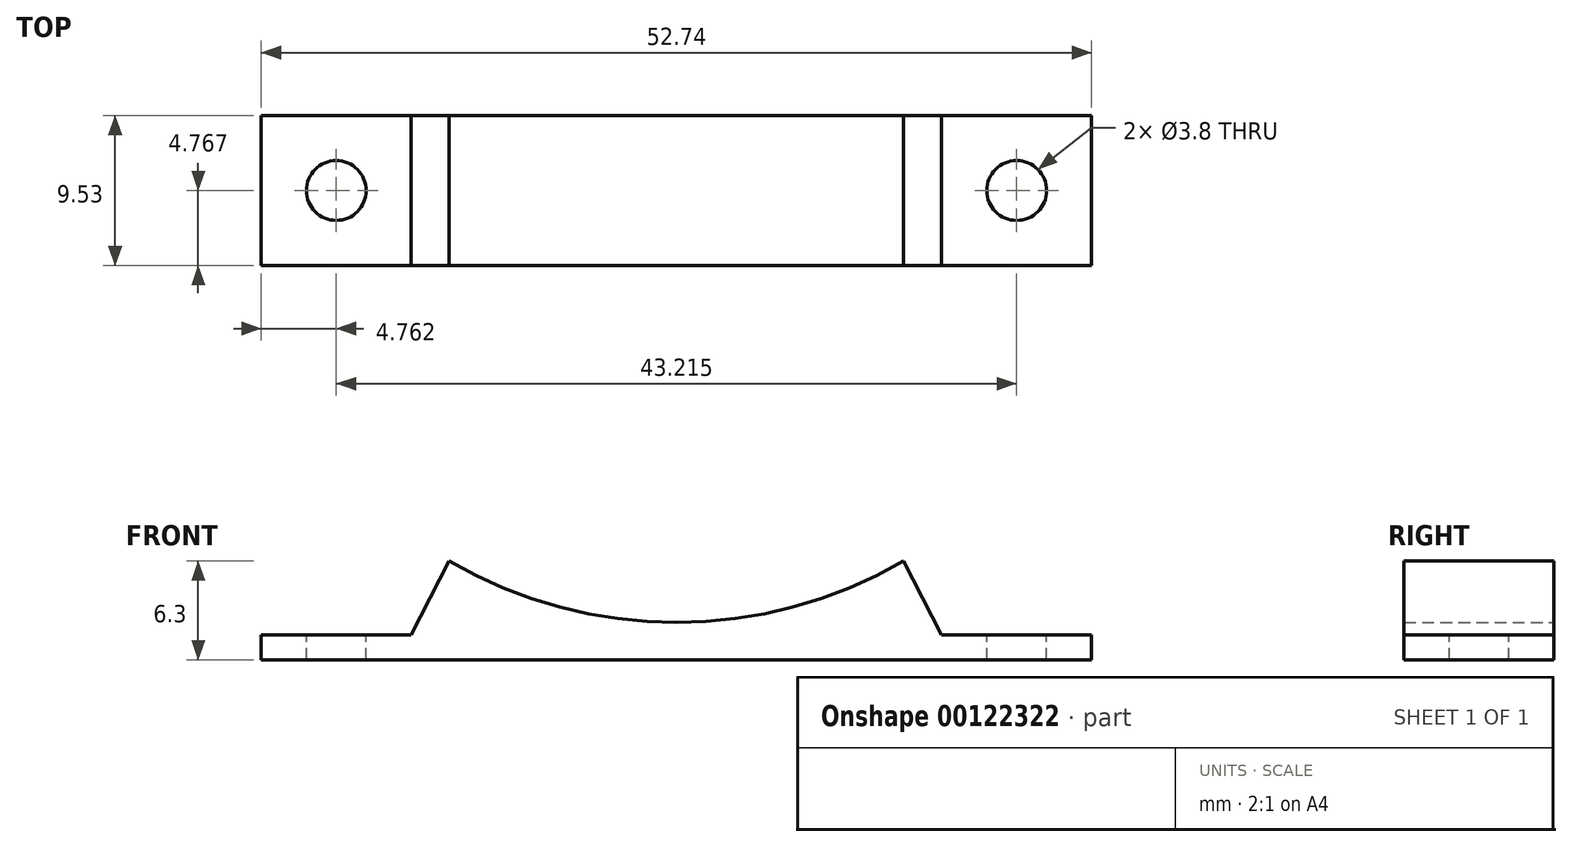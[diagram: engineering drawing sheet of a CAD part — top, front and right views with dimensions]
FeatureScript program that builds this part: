
annotation { "Feature Type Name" : "Feature", "Feature Type Description" : "" }
export const myFeature = defineFeature(function(context is Context, id is Id, definition is map)
    precondition{}
    {
        {
            var Q0;
            Q0=qCreatedBy(makeId("Front.planeOp"),FACE);
            var sketch = newSketch(context, id + "F0", { "sketchPlane" : qUnion([Q0])});
            skCircle(sketch, "E0", {"center": v(0, 0) * mm, "radius": 28.58 * mm});
            skLineSegment(sketch, "E1", {"start": v(0, -30.96) * mm, "end": v(-15.88, -30.96) * mm});
            skLineSegment(sketch, "E2", {"start": v(0, -30.96) * mm, "end": v(15.88, -30.96) * mm});
            skLineSegment(sketch, "E3", {"start": v(15.88, -30.96) * mm, "end": v(0, 0) * mm});
            skLineSegment(sketch, "E4", {"start": v(-15.88, -30.96) * mm, "end": v(0, 0) * mm});
            skLineSegment(sketch, "E5", {"start": v(-15.88, -30.96) * mm, "end": v(-26.37, -30.96) * mm});
            skLineSegment(sketch, "E6", {"start": v(-26.37, -30.96) * mm, "end": v(-26.37, -29.37) * mm});
            skLineSegment(sketch, "E7", {"start": v(-26.37, -29.37) * mm, "end": v(-16.84, -29.37) * mm});
            skLineSegment(sketch, "E8", {"start": v(-16.84, -29.37) * mm, "end": v(-14.43, -24.66) * mm});
            skCircle(sketch, "E9", {"center": v(0, 0) * mm, "radius": 30.16 * mm});
            skLineSegment(sketch, "E10", {"start": v(15.88, -30.96) * mm, "end": v(26.37, -30.96) * mm});
            skLineSegment(sketch, "E11", {"start": v(26.37, -30.96) * mm, "end": v(26.37, -29.37) * mm});
            skLineSegment(sketch, "E12", {"start": v(26.37, -29.37) * mm, "end": v(16.84, -29.37) * mm});
            skLineSegment(sketch, "E13", {"start": v(16.84, -29.37) * mm, "end": v(14.43, -24.66) * mm});
            skSolve(sketch);
        }
        {
            var Q0;
            {var subQ0=sQuery(id+"F0.wireOp",EDGE,"E4");var subQ1=sQuery(id+"F0.wireOp",EDGE,"E0");var subQ2=makeQuery(id+"F0.imprint","INTERSECT",VERTEX,{"derivedFrom":[subQ1,subQ0]});Q0=makeQuery(id+"F0.imprint","IMPRINT",FACE,{"disambiguationData":[TD([[makeQuery(id+"F0.imprint","IMPRINT",EDGE,{"disambiguationData":[TD([[subQ2,-1.0]])],"derivedFrom":subQ1}),-1.0]])]});}
            var Q1;
            {var subQ0=sQuery(id+"F0.wireOp",EDGE,"E13");var subQ1=sQuery(id+"F0.wireOp",EDGE,"E0");var subQ2=makeQuery(id+"F0.imprint","INTERSECT",VERTEX,{"derivedFrom":[subQ1,subQ0]});Q1=makeQuery(id+"F0.imprint","IMPRINT",FACE,{"disambiguationData":[TD([[makeQuery(id+"F0.imprint","IMPRINT",EDGE,{"disambiguationData":[TD([[subQ2,1.0]])],"derivedFrom":subQ1}),-1.0]])]});}
            var Q2;
            {var subQ0=sQuery(id+"F0.wireOp",EDGE,"E10");Q2=makeQuery(id+"F0.imprint","IMPRINT",FACE,{"disambiguationData":[TD([[makeQuery(id+"F0.imprint","IMPRINT",EDGE,{"derivedFrom":subQ0}),1.0]])]});}
            var Q3;
            {var subQ0=sQuery(id+"F0.wireOp",EDGE,"E8");var subQ1=sQuery(id+"F0.wireOp",EDGE,"E0");var subQ2=makeQuery(id+"F0.imprint","INTERSECT",VERTEX,{"derivedFrom":[subQ1,subQ0]});Q3=makeQuery(id+"F0.imprint","IMPRINT",FACE,{"disambiguationData":[TD([[makeQuery(id+"F0.imprint","IMPRINT",EDGE,{"disambiguationData":[TD([[subQ2,-1.0]])],"derivedFrom":subQ1}),-1.0]])]});}
            var Q4;
            {var subQ6=sQuery(id+"F0.wireOp",EDGE,"E5");Q4=makeQuery(id+"F0.imprint","IMPRINT",FACE,{"disambiguationData":[TD([[makeQuery(id+"F0.imprint","IMPRINT",EDGE,{"derivedFrom":subQ6}),-1.0]])]});}
            extrude(context, id + "F1", {"entities" : qUnion([Q0, Q1, Q2, Q3, Q4]), "depth" : 9.52 * mm});
        }
        {
            var Q0;
            Q0=makeQuery(id+"F1.opExtrude","SWEPT_FACE",FACE,{"disambiguationData":[OSD([sQuery(id+"F0.wireOp",EDGE,"E12")])]});
            var sketch = newSketch(context, id + "F2", { "sketchPlane" : qUnion([Q0])});
            skCircle(sketch, "E14", {"center": v(21.6, -4.76) * mm, "radius": 1.9 * mm});
            skPoint(sketch, "E14.centerSnap0", {"position": v(26.37, -4.76) * mm});
            skCircle(sketch, "E15", {"center": v(-21.6, -4.76) * mm, "radius": 1.9 * mm});
            skSolve(sketch);
        }
        {
            var Q0;
            Q0=makeQuery(id+"F2.imprint","IMPRINT",FACE,{"disambiguationData":[TD([[makeQuery(id+"F2.imprint","IMPRINT",EDGE,{"derivedFrom":sQuery(id+"F2.wireOp",EDGE,"E14")}),1.0]])]});
            var Q1;
            Q1=makeQuery(id+"F2.imprint","IMPRINT",FACE,{"disambiguationData":[TD([[makeQuery(id+"F2.imprint","IMPRINT",EDGE,{"derivedFrom":sQuery(id+"F2.wireOp",EDGE,"E15")}),1.0]])]});
            extrude(context, id + "F3", {"entities" : qUnion([Q0, Q1]), "operationType" : NewBodyOperationType.REMOVE, "endBound" : BoundingType.THROUGH_ALL, "oppositeDirection" : true, "depth" : 25.4 * mm});
        }
        {
            var Q0;
            Q0=makeQuery(id+"F1.opExtrude","CAP_FACE",FACE,{"disambiguationData":[OSD([sQuery(id+"F0.wireOp",EDGE,"E0"),sQuery(id+"F0.wireOp",EDGE,"E3"),sQuery(id+"F0.wireOp",EDGE,"E4"),sQuery(id+"F0.wireOp",EDGE,"E5"),sQuery(id+"F0.wireOp",EDGE,"E6"),sQuery(id+"F0.wireOp",EDGE,"E7"),sQuery(id+"F0.wireOp",EDGE,"E8"),sQuery(id+"F0.wireOp",EDGE,"E9"),sQuery(id+"F0.wireOp",EDGE,"E10"),sQuery(id+"F0.wireOp",EDGE,"E11"),sQuery(id+"F0.wireOp",EDGE,"E12"),sQuery(id+"F0.wireOp",EDGE,"E13")])],"isStart":false});
            var sketch = newSketch(context, id + "F4", { "sketchPlane" : qUnion([Q0])});
            skLineSegment(sketch, "E16", {"start": v(-15.88, -30.96) * mm, "end": v(15.88, -30.96) * mm});
            skSolve(sketch);
        }
        {
            var Q0;
            Q0=makeQuery(id+"F4.imprint","IMPRINT",FACE,{"disambiguationData":[TD([[makeQuery(id+"F4.imprint","IMPRINT",EDGE,{"derivedFrom":sQuery(id+"F4.wireOp",EDGE,"E16")}),1.0]])]});
            var Q1;
            Q1=makeQuery(id+"F1.opExtrude","CAP_FACE",FACE,{"disambiguationData":[OSD([sQuery(id+"F0.wireOp",EDGE,"E0"),sQuery(id+"F0.wireOp",EDGE,"E3"),sQuery(id+"F0.wireOp",EDGE,"E4"),sQuery(id+"F0.wireOp",EDGE,"E5"),sQuery(id+"F0.wireOp",EDGE,"E6"),sQuery(id+"F0.wireOp",EDGE,"E7"),sQuery(id+"F0.wireOp",EDGE,"E8"),sQuery(id+"F0.wireOp",EDGE,"E9"),sQuery(id+"F0.wireOp",EDGE,"E10"),sQuery(id+"F0.wireOp",EDGE,"E11"),sQuery(id+"F0.wireOp",EDGE,"E12"),sQuery(id+"F0.wireOp",EDGE,"E13")])],"isStart":true});
            extrude(context, id + "F5", {"entities" : qUnion([Q0]), "operationType" : NewBodyOperationType.ADD, "endBound" : BoundingType.UP_TO_SURFACE, "oppositeDirection" : true, "depth" : 25.4 * mm, "endBoundEntityFace" : qUnion([Q1]), "offsetDistance" : 25.4 * mm});
        }
    });
